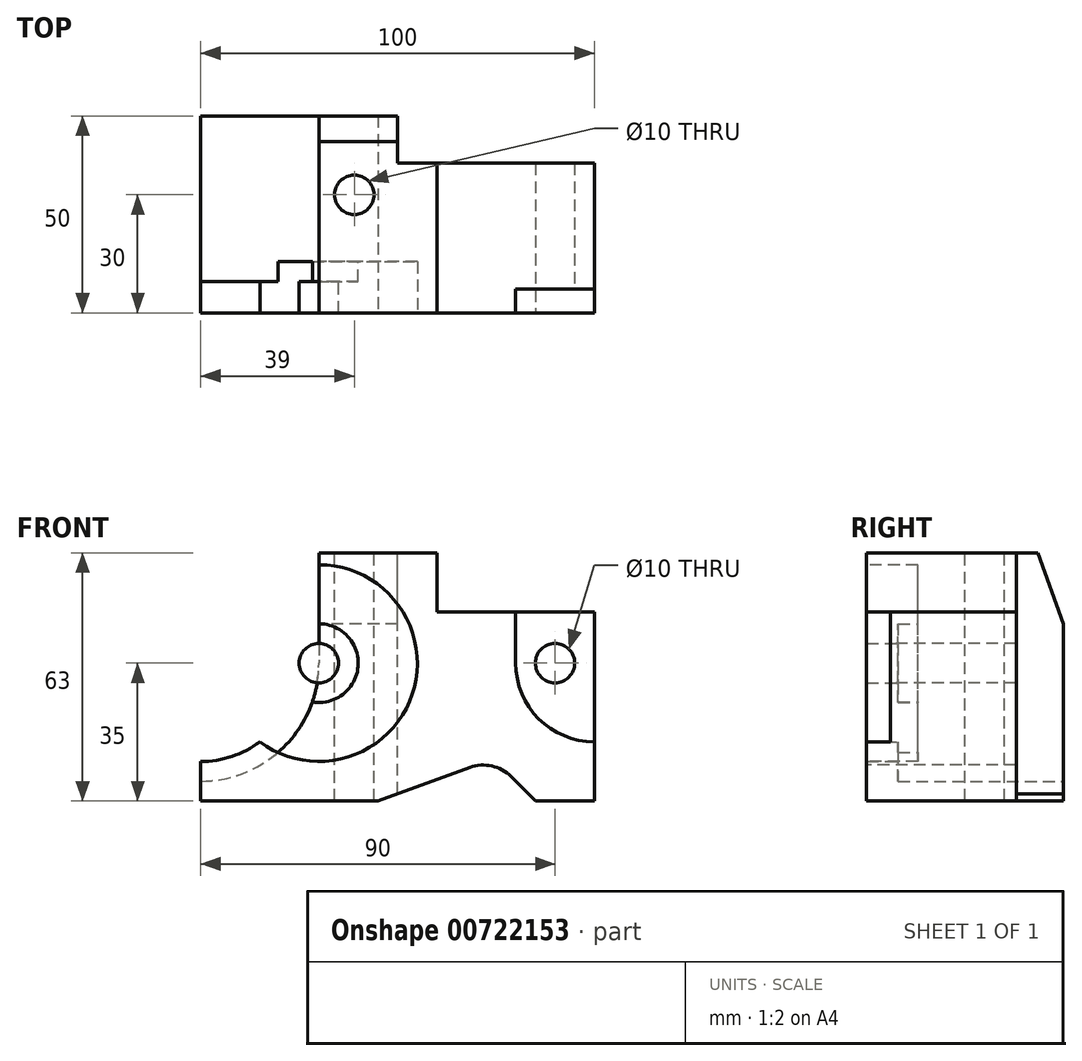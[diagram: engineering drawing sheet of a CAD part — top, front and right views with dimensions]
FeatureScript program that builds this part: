
annotation { "Feature Type Name" : "Feature", "Feature Type Description" : "" }
export const myFeature = defineFeature(function(context is Context, id is Id, definition is map)
    precondition{}
    {
        {
            var Q0;
            Q0=qCreatedBy(makeId("Front.planeOp"),FACE);
            var sketch = newSketch(context, id + "F0", { "sketchPlane" : qUnion([Q0])});
            skLineSegment(sketch, "E0.bottom", {"start": v(0, 0) * mm, "end": v(100, 0) * mm});
            skLineSegment(sketch, "E0.top", {"start": v(0, 63) * mm, "end": v(100, 63) * mm});
            skLineSegment(sketch, "E0.left", {"start": v(0, 0) * mm, "end": v(0, 63) * mm});
            skLineSegment(sketch, "E0.right", {"start": v(100, 0) * mm, "end": v(100, 63) * mm});
            skSolve(sketch);
        }
        {
            var Q0;
            Q0 = qSketchRegion(id + "F0", true);
            extrude(context, id + "F1", {"entities" : qUnion([Q0]), "depth" : 50 * mm, "offsetDistance" : 25 * mm});
        }
        {
            var Q0;
            Q0=makeQuery(id+"F1.opExtrude","CAP_FACE",FACE,{"disambiguationData":[OSD([sQuery(id+"F0.wireOp",EDGE,"E0.bottom"),sQuery(id+"F0.wireOp",EDGE,"E0.top"),sQuery(id+"F0.wireOp",EDGE,"E0.left"),sQuery(id+"F0.wireOp",EDGE,"E0.right")])],"isStart":false});
            var sketch = newSketch(context, id + "F2", { "sketchPlane" : qUnion([Q0])});
            skLineSegment(sketch, "E1.bottom", {"start": v(100, 63) * mm, "end": v(60, 63) * mm});
            skLineSegment(sketch, "E1.top", {"start": v(100, 48) * mm, "end": v(60, 48) * mm});
            skLineSegment(sketch, "E1.left", {"start": v(100, 63) * mm, "end": v(100, 48) * mm});
            skLineSegment(sketch, "E1.right", {"start": v(60, 63) * mm, "end": v(60, 48) * mm});
            skLineSegment(sketch, "E2", {"start": v(100, 0) * mm, "end": v(85, 0) * mm});
            skLineSegment(sketch, "E3", {"start": v(85, 0) * mm, "end": v(45, 0) * mm});
            skLineSegment(sketch, "E4", {"start": v(45, 0) * mm, "end": v(68.34, 8.5) * mm});
            skLineSegment(sketch, "E5", {"start": v(85, 0) * mm, "end": v(78.83, 6.17) * mm});
            skArc(sketch, "E6.filletArc", {"start": v(78.83, 6.17) * mm, "mid": v(73.92, 8.86) * mm, "end": v(68.34, 8.5) * mm});
            skSolve(sketch);
        }
        {
            var Q0;
            Q0 = qSketchRegion(id + "F2", true);
            var Q1;
            Q1=makeQuery(id+"F2.imprint","IMPRINT",FACE,{"disambiguationData":[TD([[makeQuery(id+"F2.imprint","IMPRINT",EDGE,{"derivedFrom":sQuery(id+"F2.wireOp",EDGE,"E3")}),1.0]])]});
            extrude(context, id + "F3", {"entities" : qUnion([Q0, Q1]), "operationType" : NewBodyOperationType.REMOVE, "endBound" : BoundingType.THROUGH_ALL, "oppositeDirection" : true, "depth" : 25 * mm, "offsetDistance" : 25 * mm});
        }
        {
            var Q0;
            Q0=makeQuery(id+"F1.opExtrude","CAP_FACE",FACE,{"disambiguationData":[OSD([sQuery(id+"F0.wireOp",EDGE,"E0.bottom"),sQuery(id+"F0.wireOp",EDGE,"E0.top"),sQuery(id+"F0.wireOp",EDGE,"E0.left"),sQuery(id+"F0.wireOp",EDGE,"E0.right")])],"isStart":false});
            var sketch = newSketch(context, id + "F4", { "sketchPlane" : qUnion([Q0])});
            skCircle(sketch, "E7", {"center": v(100, 35) * mm, "radius": 20 * mm});
            skLineSegment(sketch, "E8.bottom", {"start": v(100, 35) * mm, "end": v(80, 35) * mm});
            skLineSegment(sketch, "E8.top", {"start": v(100, 48) * mm, "end": v(80, 48) * mm});
            skLineSegment(sketch, "E8.left", {"start": v(100, 35) * mm, "end": v(100, 48) * mm});
            skLineSegment(sketch, "E8.right", {"start": v(80, 35) * mm, "end": v(80, 48) * mm});
            skSolve(sketch);
        }
        {
            var Q0;
            {var subQ0=sQuery(id+"F4.wireOp",EDGE,"E8.bottom");Q0=makeQuery(id+"F4.imprint","IMPRINT",FACE,{"disambiguationData":[TD([[makeQuery(id+"F4.imprint","IMPRINT",EDGE,{"derivedFrom":subQ0}),-1.0]])]});}
            var Q1;
            {var subQ0=sQuery(id+"F4.wireOp",EDGE,"E8.right");Q1=makeQuery(id+"F4.imprint","IMPRINT",FACE,{"disambiguationData":[TD([[makeQuery(id+"F4.imprint","IMPRINT",EDGE,{"derivedFrom":subQ0}),-1.0]])]});}
            var Q2;
            {var subQ0=sQuery(id+"F4.wireOp",EDGE,"E8.bottom");Q2=makeQuery(id+"F4.imprint","IMPRINT",FACE,{"disambiguationData":[TD([[makeQuery(id+"F4.imprint","IMPRINT",EDGE,{"derivedFrom":subQ0}),1.0]])]});}
            extrude(context, id + "F5", {"entities" : qUnion([Q0, Q1, Q2]), "operationType" : NewBodyOperationType.REMOVE, "oppositeDirection" : true, "depth" : 6 * mm, "offsetDistance" : 25 * mm});
        }
        {
            var Q0;
            Q0=makeQuery(id+"F5.boolean.opBoolean","COPY",FACE,{"derivedFrom":makeQuery(id+"F5.opExtrude","CAP_FACE",FACE,{"disambiguationData":[OSD([sQuery(id+"F0.wireOp",EDGE,"E0.right"),sQuery(id+"F4.wireOp",EDGE,"E7"),sQuery(id+"F4.wireOp",EDGE,"E8.top"),sQuery(id+"F4.wireOp",EDGE,"E8.left"),sQuery(id+"F4.wireOp",EDGE,"E8.right")])],"isStart":false})});
            var sketch = newSketch(context, id + "F6", { "sketchPlane" : qUnion([Q0])});
            skCircle(sketch, "E9", {"center": v(90, 35) * mm, "radius": 5 * mm});
            skSolve(sketch);
        }
        {
            var Q0;
            Q0 = qSketchRegion(id + "F6", true);
            extrude(context, id + "F7", {"entities" : qUnion([Q0]), "operationType" : NewBodyOperationType.REMOVE, "endBound" : BoundingType.THROUGH_ALL, "oppositeDirection" : true, "depth" : 25 * mm, "offsetDistance" : 25 * mm});
        }
        {
            var Q0;
            Q0=makeQuery(id+"F1.opExtrude","CAP_FACE",FACE,{"disambiguationData":[OSD([sQuery(id+"F0.wireOp",EDGE,"E0.bottom"),sQuery(id+"F0.wireOp",EDGE,"E0.top"),sQuery(id+"F0.wireOp",EDGE,"E0.left"),sQuery(id+"F0.wireOp",EDGE,"E0.right")])],"isStart":false});
            var sketch = newSketch(context, id + "F8", { "sketchPlane" : qUnion([Q0])});
            skCircle(sketch, "E10", {"center": v(30, 35) * mm, "radius": 25 * mm});
            skSolve(sketch);
        }
        {
            var Q0;
            Q0=makeQuery(id+"F8.imprint","IMPRINT",FACE,{"disambiguationData":[TD([[makeQuery(id+"F8.imprint","IMPRINT",EDGE,{"derivedFrom":sQuery(id+"F8.wireOp",EDGE,"E10")}),1.0]])]});
            extrude(context, id + "F9", {"entities" : qUnion([Q0]), "operationType" : NewBodyOperationType.REMOVE, "oppositeDirection" : true, "depth" : 13 * mm, "offsetDistance" : 25 * mm});
        }
        {
            var Q0;
            Q0=makeQuery(id+"F9.boolean.opBoolean","COPY",FACE,{"derivedFrom":makeQuery(id+"F9.opExtrude","CAP_FACE",FACE,{"disambiguationData":[OSD([sQuery(id+"F8.wireOp",EDGE,"E10")])],"isStart":false})});
            var sketch = newSketch(context, id + "F10", { "sketchPlane" : qUnion([Q0])});
            skCircle(sketch, "E11", {"center": v(30, 35) * mm, "radius": 10 * mm});
            skSolve(sketch);
        }
        {
            var Q0;
            Q0 = qSketchRegion(id + "F10", true);
            extrude(context, id + "F11", {"entities" : qUnion([Q0]), "operationType" : NewBodyOperationType.ADD, "depth" : 5 * mm, "offsetDistance" : 25 * mm});
        }
        {
            var Q0;
            Q0=makeQuery(id+"F1.opExtrude","CAP_FACE",FACE,{"disambiguationData":[OSD([sQuery(id+"F0.wireOp",EDGE,"E0.bottom"),sQuery(id+"F0.wireOp",EDGE,"E0.top"),sQuery(id+"F0.wireOp",EDGE,"E0.left"),sQuery(id+"F0.wireOp",EDGE,"E0.right")])],"isStart":true});
            var sketch = newSketch(context, id + "F12", { "sketchPlane" : qUnion([Q0])});
            skCircle(sketch, "E12", {"center": v(0, 35) * mm, "radius": 30 * mm});
            skLineSegment(sketch, "E13.bottom", {"start": v(0, 63) * mm, "end": v(-30, 63) * mm});
            skLineSegment(sketch, "E13.top", {"start": v(0, 35) * mm, "end": v(-30, 35) * mm});
            skLineSegment(sketch, "E13.left", {"start": v(0, 63) * mm, "end": v(0, 35) * mm});
            skLineSegment(sketch, "E13.right", {"start": v(-30, 63) * mm, "end": v(-30, 35) * mm});
            skSolve(sketch);
        }
        {
            var Q0;
            {var subQ0=sQuery(id+"F12.wireOp",EDGE,"E13.right");Q0=makeQuery(id+"F12.imprint","IMPRINT",FACE,{"disambiguationData":[TD([[makeQuery(id+"F12.imprint","IMPRINT",EDGE,{"derivedFrom":subQ0}),1.0]])]});}
            var Q1;
            {var subQ0=sQuery(id+"F12.wireOp",EDGE,"E13.top");Q1=makeQuery(id+"F12.imprint","IMPRINT",FACE,{"disambiguationData":[TD([[makeQuery(id+"F12.imprint","IMPRINT",EDGE,{"derivedFrom":subQ0}),-1.0]])]});}
            var Q2;
            {var subQ0=sQuery(id+"F12.wireOp",EDGE,"E13.top");Q2=makeQuery(id+"F12.imprint","IMPRINT",FACE,{"disambiguationData":[TD([[makeQuery(id+"F12.imprint","IMPRINT",EDGE,{"derivedFrom":subQ0}),1.0]])]});}
            extrude(context, id + "F13", {"entities" : qUnion([Q0, Q1, Q2]), "operationType" : NewBodyOperationType.REMOVE, "oppositeDirection" : true, "depth" : 42 * mm, "offsetDistance" : 25 * mm});
        }
        {
            var Q0;
            Q0=makeQuery(id+"F1.opExtrude","CAP_FACE",FACE,{"disambiguationData":[OSD([sQuery(id+"F0.wireOp",EDGE,"E0.bottom"),sQuery(id+"F0.wireOp",EDGE,"E0.top"),sQuery(id+"F0.wireOp",EDGE,"E0.left"),sQuery(id+"F0.wireOp",EDGE,"E0.right")])],"isStart":true});
            var sketch = newSketch(context, id + "F14", { "sketchPlane" : qUnion([Q0])});
            skCircle(sketch, "E14", {"center": v(0, 35) * mm, "radius": 25 * mm});
            skLineSegment(sketch, "E15.0", {"start": v(0, 63) * mm, "end": v(-30, 63) * mm});
            skLineSegment(sketch, "E15.1", {"start": v(0, 5) * mm, "end": v(0, 63) * mm});
            skLineSegment(sketch, "E16.top", {"start": v(0, 35) * mm, "end": v(-30, 35) * mm});
            skLineSegment(sketch, "E16.left", {"start": v(0, 63) * mm, "end": v(0, 35) * mm});
            skLineSegment(sketch, "E16.right", {"start": v(-30, 63) * mm, "end": v(-30, 35) * mm});
            skSolve(sketch);
        }
        {
            var Q0;
            Q0 = qSketchRegion(id + "F14", true);
            extrude(context, id + "F15", {"entities" : qUnion([Q0]), "operationType" : NewBodyOperationType.REMOVE, "endBound" : BoundingType.THROUGH_ALL, "oppositeDirection" : true, "depth" : 25 * mm, "offsetDistance" : 25 * mm});
        }
        {
            var Q0;
            Q0=makeQuery(id+"F11.opExtrude","CAP_FACE",FACE,{"disambiguationData":[OSD([sQuery(id+"F10.wireOp",EDGE,"E11")])],"isStart":false});
            var sketch = newSketch(context, id + "F16", { "sketchPlane" : qUnion([Q0])});
            skCircle(sketch, "E17", {"center": v(30, 35) * mm, "radius": 5 * mm});
            skSolve(sketch);
        }
        {
            var Q0;
            {var subQ0=sQuery(id+"F16.wireOp",EDGE,"E17");var subQ1=makeQuery(id+"F11.opExtrude","CAP_FACE",FACE,{"disambiguationData":[OSD([sQuery(id+"F10.wireOp",EDGE,"E11")])],"isStart":false});var subQ2=sQuery(id+"F12.wireOp",EDGE,"E12");var subQ3=makeQuery(id+"F13.boolean.opBoolean","COPY",EDGE,{"disambiguationData":[topologyDisambiguationEdgeConnected([subQ1])],"derivedFrom":makeQuery(id+"F13.opExtrude","CAP_EDGE",EDGE,{"disambiguationData":[OSD([subQ2])],"isStart":false})});var subQ4=makeQuery(id+"F16.imprint","INTERSECT",VERTEX,{"derivedFrom":[subQ3,subQ0]});Q0=makeQuery(id+"F16.imprint","IMPRINT",FACE,{"disambiguationData":[TD([[makeQuery(id+"F16.imprint","IMPRINT",EDGE,{"disambiguationData":[TD([[subQ4,-1.0]])],"derivedFrom":subQ0}),1.0]])]});}
            var Q1;
            {var subQ0=sQuery(id+"F16.wireOp",EDGE,"E17");var subQ1=makeQuery(id+"F11.opExtrude","CAP_FACE",FACE,{"disambiguationData":[OSD([sQuery(id+"F10.wireOp",EDGE,"E11")])],"isStart":false});var subQ2=sQuery(id+"F12.wireOp",EDGE,"E12");var subQ3=makeQuery(id+"F13.boolean.opBoolean","COPY",EDGE,{"disambiguationData":[topologyDisambiguationEdgeConnected([subQ1])],"derivedFrom":makeQuery(id+"F13.opExtrude","CAP_EDGE",EDGE,{"disambiguationData":[OSD([subQ2])],"isStart":false})});var subQ4=makeQuery(id+"F16.imprint","INTERSECT",VERTEX,{"derivedFrom":[subQ3,subQ0]});Q1=makeQuery(id+"F16.imprint","IMPRINT",FACE,{"disambiguationData":[TD([[makeQuery(id+"F16.imprint","IMPRINT",EDGE,{"disambiguationData":[TD([[subQ4,1.0]])],"derivedFrom":subQ0}),1.0]])]});}
            var Q2;
            Q2=makeQuery(id+"F1.opExtrude","CAP_FACE",FACE,{"disambiguationData":[OSD([sQuery(id+"F0.wireOp",EDGE,"E0.bottom"),sQuery(id+"F0.wireOp",EDGE,"E0.top"),sQuery(id+"F0.wireOp",EDGE,"E0.left"),sQuery(id+"F0.wireOp",EDGE,"E0.right")])],"isStart":false});
            extrude(context, id + "F17", {"entities" : qUnion([Q0, Q1]), "operationType" : NewBodyOperationType.ADD, "endBound" : BoundingType.UP_TO_SURFACE, "depth" : 8 * mm, "endBoundEntityFace" : qUnion([Q2]), "offsetDistance" : 25 * mm});
        }
        {
            var Q0;
            Q0=makeQuery(id+"F1.opExtrude","SWEPT_FACE",FACE,{"disambiguationData":[OSD([sQuery(id+"F0.wireOp",EDGE,"E0.top")])]});
            var sketch = newSketch(context, id + "F18", { "sketchPlane" : qUnion([Q0])});
            skLineSegment(sketch, "E18.0", {"start": v(100, 0) * mm, "end": v(60, 0) * mm});
            skLineSegment(sketch, "E18.1", {"start": v(100, 0) * mm, "end": v(100, -44) * mm});
            skLineSegment(sketch, "E19.0", {"start": v(30, 0) * mm, "end": v(60, 0) * mm});
            skLineSegment(sketch, "E20.bottom", {"start": v(100, 0) * mm, "end": v(50, 0) * mm});
            skLineSegment(sketch, "E20.top", {"start": v(100, -12) * mm, "end": v(50, -12) * mm});
            skLineSegment(sketch, "E20.left", {"start": v(100, 0) * mm, "end": v(100, -12) * mm});
            skLineSegment(sketch, "E20.right", {"start": v(50, 0) * mm, "end": v(50, -12) * mm});
            skSolve(sketch);
        }
        {
            var Q0;
            Q0 = qSketchRegion(id + "F18", true);
            extrude(context, id + "F19", {"entities" : qUnion([Q0]), "operationType" : NewBodyOperationType.REMOVE, "endBound" : BoundingType.THROUGH_ALL, "oppositeDirection" : true, "depth" : 25 * mm, "offsetDistance" : 25 * mm});
        }
        {
            var Q0;
            Q0=makeQuery(id+"F1.opExtrude","SWEPT_FACE",FACE,{"disambiguationData":[OSD([sQuery(id+"F0.wireOp",EDGE,"E0.top")])]});
            var sketch = newSketch(context, id + "F20", { "sketchPlane" : qUnion([Q0])});
            skCircle(sketch, "E21", {"center": v(39, -20) * mm, "radius": 5 * mm});
            skSolve(sketch);
        }
        {
            var Q0;
            Q0 = qSketchRegion(id + "F20", true);
            extrude(context, id + "F21", {"entities" : qUnion([Q0]), "operationType" : NewBodyOperationType.REMOVE, "endBound" : BoundingType.THROUGH_ALL, "oppositeDirection" : true, "depth" : 25 * mm, "offsetDistance" : 25 * mm});
        }
        {
            var Q0;
            Q0=makeQuery(id+"F15.boolean.opBoolean","MERGE",FACE,{"derivedFrom":[makeQuery(id+"F13.boolean.opBoolean","COPY",FACE,{"derivedFrom":makeQuery(id+"F13.opExtrude","SWEPT_FACE",FACE,{"disambiguationData":[OSD([sQuery(id+"F12.wireOp",EDGE,"E13.right")])]})}),makeQuery(id+"F15.opExtrude","SWEPT_FACE",FACE,{"disambiguationData":[OSD([sQuery(id+"F14.wireOp",EDGE,"E16.right")])]})]});
            var sketch = newSketch(context, id + "F22", { "sketchPlane" : qUnion([Q0])});
            skLineSegment(sketch, "E22", {"start": v(0, 63) * mm, "end": v(0, 45) * mm});
            skLineSegment(sketch, "E23", {"start": v(0, 45) * mm, "end": v(6.55, 63) * mm});
            skSolve(sketch);
        }
        {
            var Q0;
            Q0 = qSketchRegion(id + "F22", true);
            var Q1;
            {var subQ0=sQuery(id+"F22.wireOp",EDGE,"E22");Q1=makeQuery(id+"F22.imprint","IMPRINT",FACE,{"disambiguationData":[TD([[makeQuery(id+"F22.imprint","IMPRINT",EDGE,{"derivedFrom":subQ0}),1.0]])]});}
            extrude(context, id + "F23", {"entities" : qUnion([Q0, Q1]), "operationType" : NewBodyOperationType.REMOVE, "endBound" : BoundingType.THROUGH_ALL, "oppositeDirection" : true, "depth" : 25 * mm, "offsetDistance" : 25 * mm});
        }
    });
